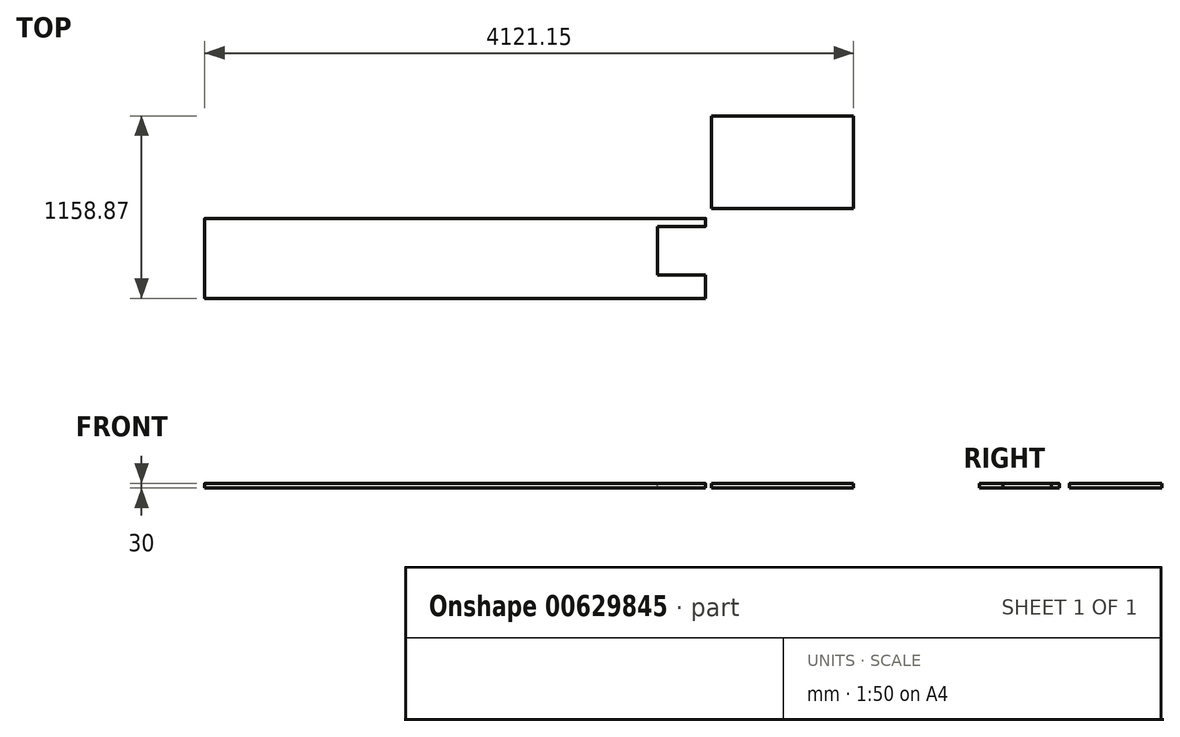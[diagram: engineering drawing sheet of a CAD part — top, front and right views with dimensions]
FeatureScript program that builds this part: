
annotation { "Feature Type Name" : "Feature", "Feature Type Description" : "" }
export const myFeature = defineFeature(function(context is Context, id is Id, definition is map)
    precondition{}
    {
        {
            var Q0;
            Q0=qCreatedBy(makeId("Top.planeOp"),FACE);
            var sketch = newSketch(context, id + "F0", { "sketchPlane" : qUnion([Q0])});
            skLineSegment(sketch, "E0.bottom", {"start": v(0, 25.4) * mm, "end": v(901.7, 25.4) * mm});
            skLineSegment(sketch, "E0.top", {"start": v(0, 612.78) * mm, "end": v(901.7, 612.78) * mm});
            skLineSegment(sketch, "E0.left", {"start": v(0, 25.4) * mm, "end": v(0, 612.78) * mm});
            skLineSegment(sketch, "E0.right", {"start": v(901.7, 25.4) * mm, "end": v(901.7, 612.78) * mm});
            skSolve(sketch);
        }
        {
            var Q0;
            Q0=makeQuery(id+"F0.imprint","IMPRINT",FACE,{"disambiguationData":[TD([[makeQuery(id+"F0.imprint","IMPRINT",EDGE,{"derivedFrom":sQuery(id+"F0.wireOp",EDGE,"E0.bottom")}),1.0]])]});
            extrude(context, id + "F1", {"entities" : qUnion([Q0]), "depth" : 30 * mm, "offsetDistance" : 25.4 * mm});
        }
        {
            var Q0;
            Q0=qCreatedBy(makeId("Top.planeOp"),FACE);
            var sketch = newSketch(context, id + "F2", { "sketchPlane" : qUnion([Q0])});
            skLineSegment(sketch, "E1.bottom", {"start": v(-38.1, -38.1) * mm, "end": v(-3219.45, -38.1) * mm});
            skLineSegment(sketch, "E1.top", {"start": v(-38.1, -546.1) * mm, "end": v(-3219.45, -546.1) * mm});
            skLineSegment(sketch, "E1.left", {"start": v(-38.1, -38.1) * mm, "end": v(-38.1, -546.1) * mm});
            skLineSegment(sketch, "E1.right", {"start": v(-3219.45, -38.1) * mm, "end": v(-3219.45, -546.1) * mm});
            skSolve(sketch);
        }
        {
            var Q0;
            Q0=makeQuery(id+"F2.imprint","IMPRINT",FACE,{"disambiguationData":[TD([[makeQuery(id+"F2.imprint","IMPRINT",EDGE,{"derivedFrom":sQuery(id+"F2.wireOp",EDGE,"E1.bottom")}),1.0]])]});
            extrude(context, id + "F3", {"entities" : qUnion([Q0]), "depth" : 30 * mm, "offsetDistance" : 25.4 * mm});
        }
        {
            var Q0;
            Q0=makeQuery(id+"F3.opExtrude","CAP_FACE",FACE,{"disambiguationData":[OSD([sQuery(id+"F2.wireOp",EDGE,"E1.bottom"),sQuery(id+"F2.wireOp",EDGE,"E1.top"),sQuery(id+"F2.wireOp",EDGE,"E1.left"),sQuery(id+"F2.wireOp",EDGE,"E1.right")])],"isStart":false});
            var sketch = newSketch(context, id + "F4", { "sketchPlane" : qUnion([Q0])});
            skLineSegment(sketch, "E2.bottom", {"start": v(-38.1, -88.9) * mm, "end": v(-342.9, -88.9) * mm});
            skLineSegment(sketch, "E2.top", {"start": v(-38.1, -396.88) * mm, "end": v(-342.9, -396.88) * mm});
            skLineSegment(sketch, "E2.left", {"start": v(-38.1, -88.9) * mm, "end": v(-38.1, -396.88) * mm});
            skLineSegment(sketch, "E2.right", {"start": v(-342.9, -88.9) * mm, "end": v(-342.9, -396.88) * mm});
            skSolve(sketch);
        }
        {
            var Q0;
            Q0=makeQuery(id+"F4.imprint","IMPRINT",FACE,{"disambiguationData":[TD([[makeQuery(id+"F4.imprint","IMPRINT",EDGE,{"derivedFrom":sQuery(id+"F4.wireOp",EDGE,"E2.bottom")}),1.0]])]});
            extrude(context, id + "F5", {"entities" : qUnion([Q0]), "operationType" : NewBodyOperationType.REMOVE, "endBound" : BoundingType.THROUGH_ALL, "oppositeDirection" : true, "depth" : 25.4 * mm, "offsetDistance" : 25.4 * mm});
        }
        {
            var Q0;
            {var subQ0=sQuery(id+"F2.wireOp",EDGE,"E1.left");var subQ1=sQuery(id+"F2.wireOp",EDGE,"E1.top");Q0=makeQuery(id+"F5.boolean.opBoolean","SPLIT",EDGE,{"disambiguationData":[TD([makeQuery(id+"F3.opExtrude","SWEPT_FACE",FACE,{"disambiguationData":[OSD([subQ1])]})])],"derivedFrom":makeQuery(id+"F3.opExtrude","CAP_EDGE",EDGE,{"disambiguationData":[OSD([subQ0])],"isStart":false})});}
            var Q1;
            Q1=makeQuery(id+"F3.opExtrude","CAP_EDGE",EDGE,{"disambiguationData":[OSD([sQuery(id+"F2.wireOp",EDGE,"E1.top")])],"isStart":false});
            var Q2;
            {var subQ0=sQuery(id+"F2.wireOp",EDGE,"E1.bottom");var subQ1=sQuery(id+"F2.wireOp",EDGE,"E1.left");Q2=makeQuery(id+"F5.boolean.opBoolean","SPLIT",EDGE,{"disambiguationData":[TD([makeQuery(id+"F3.opExtrude","SWEPT_FACE",FACE,{"disambiguationData":[OSD([subQ0])]})])],"derivedFrom":makeQuery(id+"F3.opExtrude","CAP_EDGE",EDGE,{"disambiguationData":[OSD([subQ1])],"isStart":false})});}
            var Q3;
            Q3=makeQuery(id+"F3.opExtrude","CAP_EDGE",EDGE,{"disambiguationData":[OSD([sQuery(id+"F2.wireOp",EDGE,"E1.bottom")])],"isStart":false});
            var Q4;
            Q4=makeQuery(id+"F1.opExtrude","CAP_EDGE",EDGE,{"disambiguationData":[OSD([sQuery(id+"F0.wireOp",EDGE,"E0.bottom")])],"isStart":false});
            fillet(context, id + "F6", {"entities" : qUnion([Q0, Q1, Q2, Q3, Q4]), "radius" : 5.08 * mm, "tangentPropagation" : true, "allowEdgeOverflow" : false});
        }
    });
